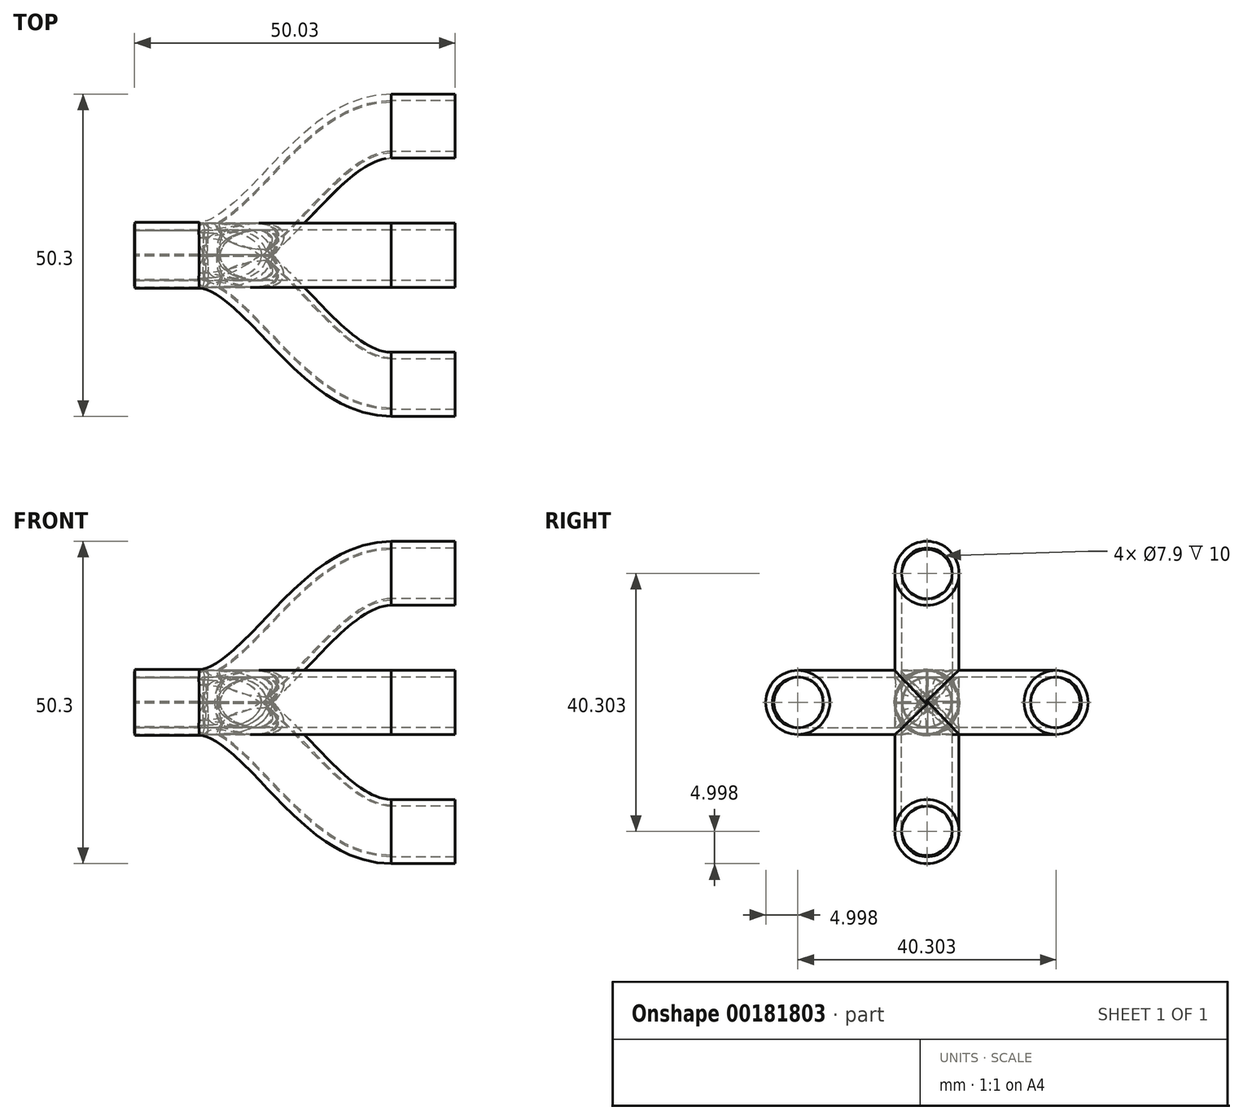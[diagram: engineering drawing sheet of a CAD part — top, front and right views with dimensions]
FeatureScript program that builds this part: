
annotation { "Feature Type Name" : "Feature", "Feature Type Description" : "" }
export const myFeature = defineFeature(function(context is Context, id is Id, definition is map)
    precondition{}
    {
        {
            var Q0;
            Q0=qCreatedBy(makeId("Top.planeOp"),FACE);
            var sketch = newSketch(context, id + "F0", { "sketchPlane" : qUnion([Q0])});
            skLineSegment(sketch, "E0", {"start": v(0, 20) * mm, "end": v(0, -20) * mm, "construction": true});
            skLineSegment(sketch, "E1", {"start": v(0, 0) * mm, "end": v(-30, 0) * mm, "construction": true});
            skFitSpline(sketch, "E2", {"points": [v(0, 20) * mm, v(-30, 0) * mm], "startDerivative": vector(-34.93, -0.21) * mm, "endDerivative": vector(-31.02, 0) * mm});
            skFitSpline(sketch, "E3.MirrorCS", {"points": [v(0, -20) * mm, v(-30, 0) * mm], "startDerivative": vector(-34.93, 0.21) * mm, "endDerivative": vector(-31.02, 0) * mm});
            skLineSegment(sketch, "E4", {"start": v(-30, 0) * mm, "end": v(-40, 0) * mm});
            skSolve(sketch);
        }
        {
            var Q0;
            Q0=qCreatedBy(makeId("Right.planeOp"),FACE);
            var sketch = newSketch(context, id + "F1", { "sketchPlane" : qUnion([Q0])});
            skCircle(sketch, "E5", {"center": v(20.15, 0) * mm, "radius": 5 * mm});
            skCircle(sketch, "E6", {"center": v(-19.93, 0) * mm, "radius": 5 * mm});
            skSolve(sketch);
        }
        {
            var Q0;
            Q0=makeQuery(id+"F1.imprint","IMPRINT",FACE,{"disambiguationData":[TD([[makeQuery(id+"F1.imprint","IMPRINT",EDGE,{"derivedFrom":sQuery(id+"F1.wireOp",EDGE,"E5")}),1.0]])]});
            var Q1;
            Q1=sQuery(id+"F0.wireOp",EDGE,"E2");
            var Q2;
            Q2=sQuery(id+"F0.wireOp",EDGE,"E4");
            sweep(context, id + "F2", {"profiles" : qUnion([Q0]), "path" : qUnion([Q1, Q2])});
        }
        {
            var Q0;
            Q0=makeQuery(id+"F1.imprint","IMPRINT",FACE,{"disambiguationData":[TD([[makeQuery(id+"F1.imprint","IMPRINT",EDGE,{"derivedFrom":sQuery(id+"F1.wireOp",EDGE,"E6")}),1.0]])]});
            var Q1;
            Q1=sQuery(id+"F0.wireOp",EDGE,"E3.MirrorCS");
            sweep(context, id + "F3", {"operationType" : NewBodyOperationType.ADD, "profiles" : qUnion([Q0]), "path" : qUnion([Q1])});
        }
        {
            var Q0;
            Q0=makeQuery(id+"F1.imprint","IMPRINT",FACE,{"disambiguationData":[TD([[makeQuery(id+"F1.imprint","IMPRINT",EDGE,{"derivedFrom":sQuery(id+"F1.wireOp",EDGE,"E6")}),1.0]])]});
            var sketch = newSketch(context, id + "F4", { "sketchPlane" : qUnion([Q0])});
            skCircle(sketch, "E7.0", {"center": v(-19.93, 0) * mm, "radius": 3.95 * mm});
            skCircle(sketch, "E8.0", {"center": v(20.15, 0) * mm, "radius": 3.95 * mm});
            skSolve(sketch);
        }
        {
            var Q0;
            Q0=makeQuery(id+"F4.imprint","IMPRINT",FACE,{"disambiguationData":[TD([[makeQuery(id+"F4.imprint","IMPRINT",EDGE,{"derivedFrom":sQuery(id+"F4.wireOp",EDGE,"E7.0")}),-1.0]])]});
            var Q1;
            Q1=sQuery(id+"F0.wireOp",EDGE,"E3.MirrorCS");
            var Q2;
            Q2=sQuery(id+"F0.wireOp",EDGE,"E4");
            sweep(context, id + "F5", {"operationType" : NewBodyOperationType.REMOVE, "profiles" : qUnion([Q0]), "path" : qUnion([Q1, Q2])});
        }
        {
            var Q0;
            Q0=makeQuery(id+"F4.imprint","IMPRINT",FACE,{"disambiguationData":[TD([[makeQuery(id+"F4.imprint","IMPRINT",EDGE,{"derivedFrom":sQuery(id+"F4.wireOp",EDGE,"E8.0")}),1.0]])]});
            var Q1;
            Q1=sQuery(id+"F0.wireOp",EDGE,"E2");
            var Q2;
            Q2=sQuery(id+"F0.wireOp",EDGE,"E4");
            sweep(context, id + "F6", {"operationType" : NewBodyOperationType.REMOVE, "profiles" : qUnion([Q0]), "path" : qUnion([Q1, Q2])});
        }
        {
            var Q0;
            Q0=makeQuery(id+"F2.opSweep","SWEPT_BODY",BODY,{"disambiguationData":[OSD([sQuery(id+"F0.wireOp",EDGE,"E4"),sQuery(id+"F1.wireOp",EDGE,"E5")])]});
            var Q1;
            Q1=sQuery(id+"F0.wireOp",EDGE,"E4");
            circularPattern(context, id + "F7", {"entities" : qUnion([Q0]), "axis" : qUnion([Q1]), "angle" : 90 * degree, "instanceCount" : 2});
        }
        {
            var Q0;
            Q0=makeQuery(id+"F4.imprint","IMPRINT",FACE,{"disambiguationData":[TD([[makeQuery(id+"F4.imprint","IMPRINT",EDGE,{"derivedFrom":sQuery(id+"F4.wireOp",EDGE,"E8.0")}),1.0]])]});
            var Q1;
            Q1=sQuery(id+"F0.wireOp",EDGE,"E2");
            sweep(context, id + "F8", {"operationType" : NewBodyOperationType.REMOVE, "profiles" : qUnion([Q0]), "path" : qUnion([Q1])});
        }
        {
            var Q0;
            Q0=makeQuery(id+"F4.imprint","IMPRINT",FACE,{"disambiguationData":[TD([[makeQuery(id+"F4.imprint","IMPRINT",EDGE,{"derivedFrom":sQuery(id+"F4.wireOp",EDGE,"E7.0")}),-1.0]])]});
            var Q1;
            Q1=sQuery(id+"F0.wireOp",EDGE,"E3.MirrorCS");
            sweep(context, id + "F9", {"operationType" : NewBodyOperationType.REMOVE, "profiles" : qUnion([Q0]), "path" : qUnion([Q1])});
        }
        {
            var Q0;
            Q0=makeQuery(id+"F7.opPattern","COPY",FACE,{"derivedFrom":makeQuery(id+"F2.opSweep","CAP_FACE",FACE,{"disambiguationData":[OSD([sQuery(id+"F0.wireOp",VERTEX,"E2.start"),sQuery(id+"F1.wireOp",EDGE,"E5")])],"isStart":true}),"instanceName":"1"});
            var sketch = newSketch(context, id + "F10", { "sketchPlane" : qUnion([Q0])});
            skCircle(sketch, "E9.0", {"center": v(0, -20.15) * mm, "radius": 5 * mm});
            skCircle(sketch, "E10.0", {"center": v(0, -20.15) * mm, "radius": 3.95 * mm});
            skSolve(sketch);
        }
        {
            var Q0;
            Q0 = qSketchRegion(id + "F10", true);
            extrude(context, id + "F11", {"entities" : qUnion([Q0]), "operationType" : NewBodyOperationType.ADD, "depth" : 10 * mm});
        }
        {
            var Q0;
            Q0=makeQuery(id+"F7.opPattern","COPY",BODY,{"derivedFrom":makeQuery(id+"F2.opSweep","SWEPT_BODY",BODY,{"disambiguationData":[OSD([sQuery(id+"F0.wireOp",EDGE,"E4"),sQuery(id+"F1.wireOp",EDGE,"E5")])]}),"instanceName":"1"});
            var Q1;
            Q1=sQuery(id+"F0.wireOp",EDGE,"E4");
            circularPattern(context, id + "F12", {"entities" : qUnion([Q0]), "axis" : qUnion([Q1]), "angle" : 90 * degree, "instanceCount" : 4});
        }
    });
